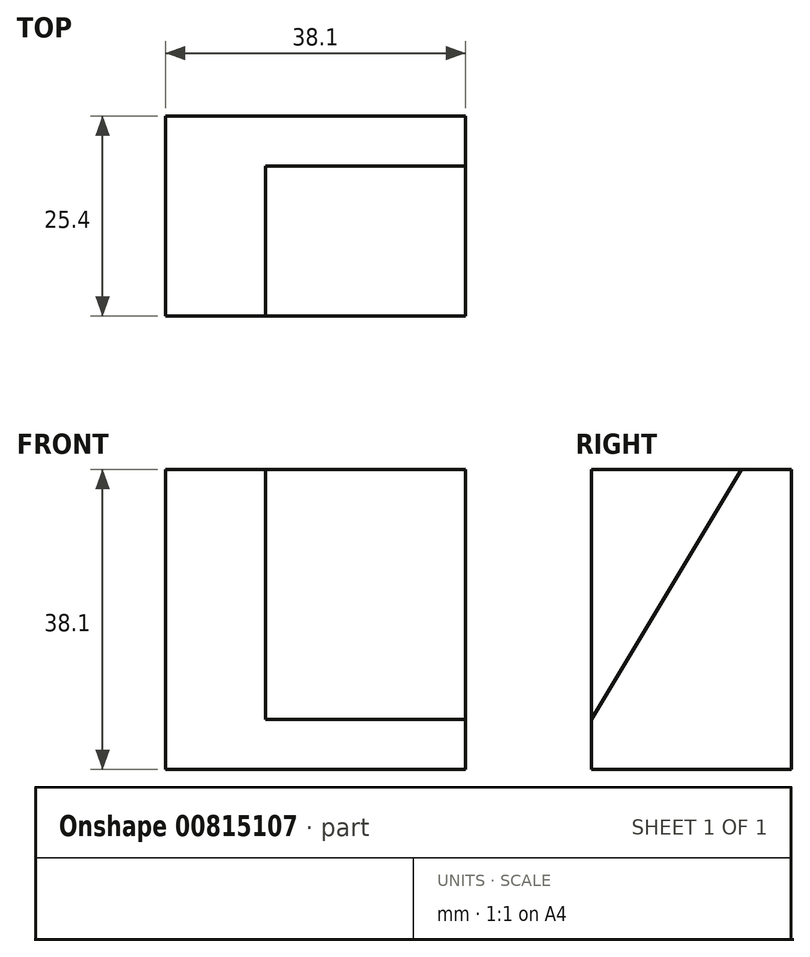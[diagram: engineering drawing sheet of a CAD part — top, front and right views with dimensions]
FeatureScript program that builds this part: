
annotation { "Feature Type Name" : "Feature", "Feature Type Description" : "" }
export const myFeature = defineFeature(function(context is Context, id is Id, definition is map)
    precondition{}
    {
        {
            var Q0;
            Q0=qCreatedBy(makeId("Top.planeOp"),FACE);
            var sketch = newSketch(context, id + "F0", { "sketchPlane" : qUnion([Q0])});
            skLineSegment(sketch, "E0.bottom", {"start": v(0, 0) * mm, "end": v(38.1, 0) * mm});
            skLineSegment(sketch, "E0.top", {"start": v(0, 25.4) * mm, "end": v(38.1, 25.4) * mm});
            skLineSegment(sketch, "E0.left", {"start": v(0, 0) * mm, "end": v(0, 25.4) * mm});
            skLineSegment(sketch, "E0.right", {"start": v(38.1, 0) * mm, "end": v(38.1, 25.4) * mm});
            skSolve(sketch);
        }
        {
            var Q0;
            Q0 = qSketchRegion(id + "F0", true);
            extrude(context, id + "F1", {"entities" : qUnion([Q0]), "depth" : 38.1 * mm, "offsetDistance" : 25.4 * mm});
        }
        {
            var Q0;
            Q0=makeQuery(id+"F1.opExtrude","SWEPT_FACE",FACE,{"disambiguationData":[OSD([sQuery(id+"F0.wireOp",EDGE,"E0.right")])]});
            var sketch = newSketch(context, id + "F2", { "sketchPlane" : qUnion([Q0])});
            skLineSegment(sketch, "E1", {"start": v(0, 0) * mm, "end": v(0, 6.35) * mm});
            skLineSegment(sketch, "E2", {"start": v(25.4, 38.1) * mm, "end": v(19.05, 38.1) * mm});
            skLineSegment(sketch, "E3", {"start": v(0, 6.35) * mm, "end": v(19.05, 38.1) * mm});
            skLineSegment(sketch, "E4", {"start": v(0, 0) * mm, "end": v(25.4, 0) * mm});
            skLineSegment(sketch, "E5", {"start": v(25.4, 0) * mm, "end": v(25.4, 38.1) * mm});
            skSolve(sketch);
        }
        {
            var Q0;
            {var subQ0=sQuery(id+"F2.wireOp",EDGE,"E3");Q0=makeQuery(id+"F2.imprint","IMPRINT",FACE,{"disambiguationData":[TD([[makeQuery(id+"F2.imprint","IMPRINT",EDGE,{"derivedFrom":subQ0}),1.0]])]});}
            extrude(context, id + "F3", {"entities" : qUnion([Q0]), "operationType" : NewBodyOperationType.REMOVE, "oppositeDirection" : true, "depth" : 25.4 * mm, "offsetDistance" : 25.4 * mm});
        }
    });
